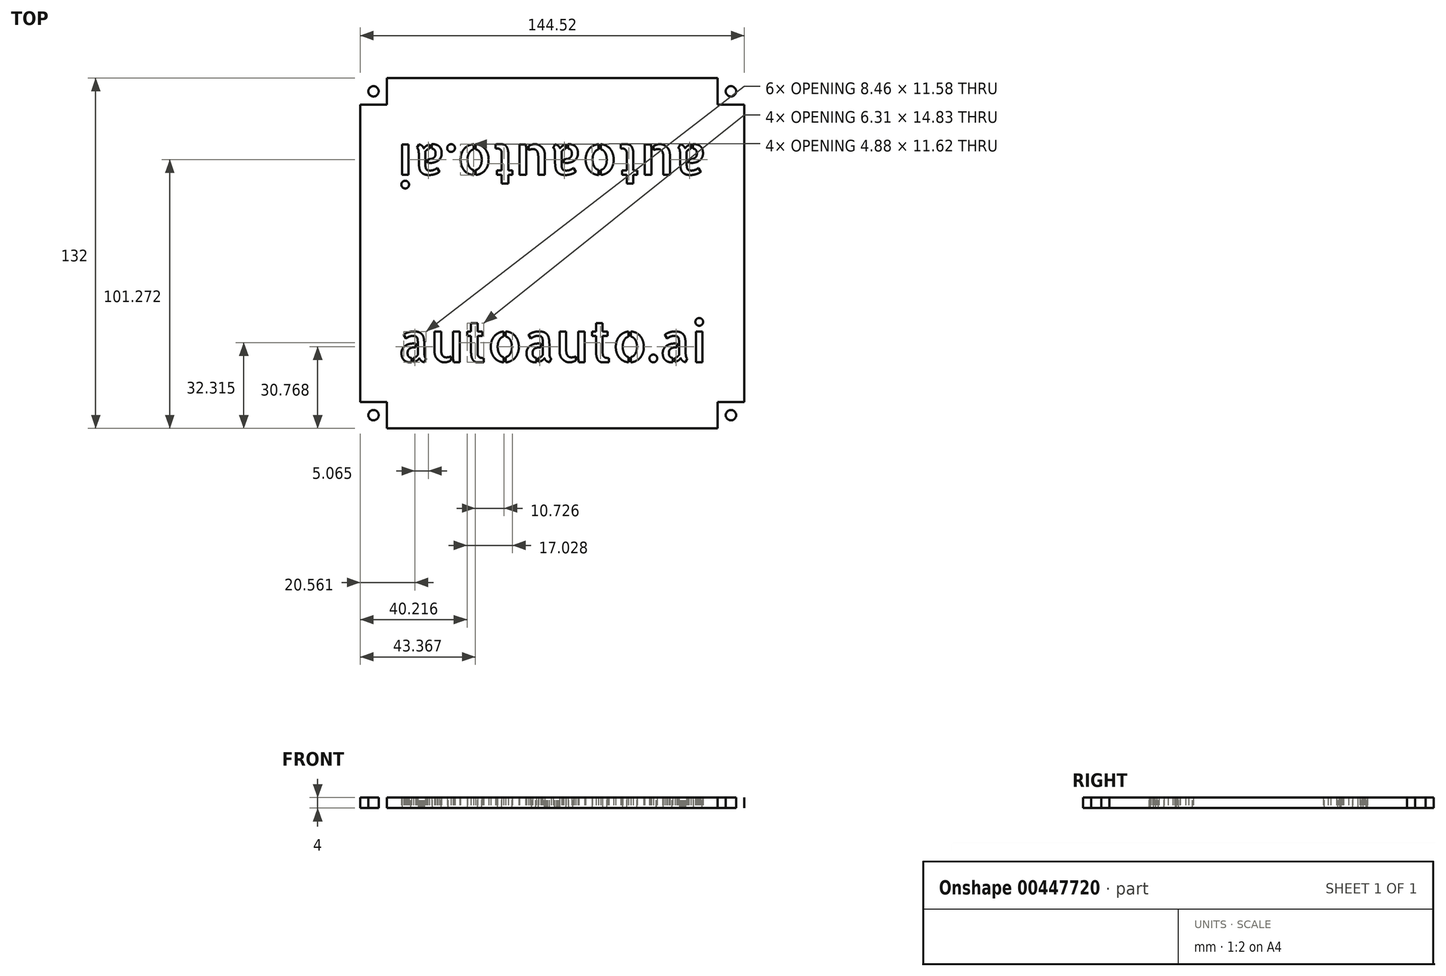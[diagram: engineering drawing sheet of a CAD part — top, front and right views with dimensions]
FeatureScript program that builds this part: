
annotation { "Feature Type Name" : "Feature", "Feature Type Description" : "" }
export const myFeature = defineFeature(function(context is Context, id is Id, definition is map)
    precondition{}
    {
        {
            var Q0;
            Q0=qCreatedBy(makeId("Top.planeOp"),FACE);
            var sketch = newSketch(context, id + "F0", { "sketchPlane" : qUnion([Q0])});
            skLineSegment(sketch, "E0.bottom", {"start": v(-72.26, 66) * mm, "end": v(72.26, 66) * mm});
            skLineSegment(sketch, "E0.top", {"start": v(-72.26, -66) * mm, "end": v(72.26, -66) * mm});
            skLineSegment(sketch, "E0.left", {"start": v(-72.26, 66) * mm, "end": v(-72.26, -66) * mm});
            skLineSegment(sketch, "E0.right", {"start": v(72.26, 66) * mm, "end": v(72.26, -66) * mm});
            skPoint(sketch, "E0.middle", {"position": v(0, 0) * mm});
            skText(sketch, "E1", { "text": "autoauto.ai", "fontName": "AllertaStencil-Regular.ttf"});
            skText(sketch, "E2", { "text": "autoauto.ai", "fontName": "AllertaStencil-Regular.ttf"});
            const initialGuessF0  = {"E1": [-0.05819, -0.041, 1, 0, 0.015], "E2": [0.05819, 0.041, -1, 0, 0.015]};
            skSetInitialGuess(sketch, initialGuessF0);
            skSolve(sketch);
        }
        {
            var Q0;
            Q0=makeQuery(id+"F0.imprint","IMPRINT",FACE,{"disambiguationData":[TD([[makeQuery(id+"F0.imprint","IMPRINT",EDGE,{"derivedFrom":sQuery(id+"F0.wireOp",EDGE,"E0.bottom")}),-1.0]])]});
            extrude(context, id + "F1", {"entities" : qUnion([Q0]), "depth" : 4 * mm});
        }
        {
            var Q0;
            Q0=makeQuery(id+"F1.opExtrude","CAP_FACE",FACE,{"disambiguationData":[OSD([sQuery(id+"F0.wireOp",EDGE,"E0.bottom"),sQuery(id+"F0.wireOp",EDGE,"E0.top"),sQuery(id+"F0.wireOp",EDGE,"E0.left"),sQuery(id+"F0.wireOp",EDGE,"E0.right"),sQuery(id+"F0.wireOp",EDGE,"E1.sketch_text.stroke-0"),sQuery(id+"F0.wireOp",EDGE,"E1.sketch_text.stroke-1"),sQuery(id+"F0.wireOp",EDGE,"E1.sketch_text.stroke-2"),sQuery(id+"F0.wireOp",EDGE,"E1.sketch_text.stroke-3"),sQuery(id+"F0.wireOp",EDGE,"E1.sketch_text.stroke-4"),sQuery(id+"F0.wireOp",EDGE,"E1.sketch_text.stroke-5"),sQuery(id+"F0.wireOp",EDGE,"E1.sketch_text.stroke-6"),sQuery(id+"F0.wireOp",EDGE,"E1.sketch_text.stroke-7"),sQuery(id+"F0.wireOp",EDGE,"E1.sketch_text.stroke-8"),sQuery(id+"F0.wireOp",EDGE,"E1.sketch_text.stroke-9"),sQuery(id+"F0.wireOp",EDGE,"E1.sketch_text.stroke-10"),sQuery(id+"F0.wireOp",EDGE,"E1.sketch_text.stroke-11"),sQuery(id+"F0.wireOp",EDGE,"E1.sketch_text.stroke-12"),sQuery(id+"F0.wireOp",EDGE,"E1.sketch_text.stroke-13"),sQuery(id+"F0.wireOp",EDGE,"E1.sketch_text.stroke-14"),sQuery(id+"F0.wireOp",EDGE,"E1.sketch_text.stroke-15"),sQuery(id+"F0.wireOp",EDGE,"E1.sketch_text.stroke-16"),sQuery(id+"F0.wireOp",EDGE,"E1.sketch_text.stroke-17"),sQuery(id+"F0.wireOp",EDGE,"E1.sketch_text.stroke-18"),sQuery(id+"F0.wireOp",EDGE,"E1.sketch_text.stroke-19"),sQuery(id+"F0.wireOp",EDGE,"E1.sketch_text.stroke-20"),sQuery(id+"F0.wireOp",EDGE,"E1.sketch_text.stroke-21"),sQuery(id+"F0.wireOp",EDGE,"E1.sketch_text.stroke-22"),sQuery(id+"F0.wireOp",EDGE,"E1.sketch_text.stroke-23"),sQuery(id+"F0.wireOp",EDGE,"E1.sketch_text.stroke-24"),sQuery(id+"F0.wireOp",EDGE,"E1.sketch_text.stroke-25"),sQuery(id+"F0.wireOp",EDGE,"E1.sketch_text.stroke-26"),sQuery(id+"F0.wireOp",EDGE,"E1.sketch_text.stroke-27"),sQuery(id+"F0.wireOp",EDGE,"E1.sketch_text.stroke-28"),sQuery(id+"F0.wireOp",EDGE,"E1.sketch_text.stroke-29"),sQuery(id+"F0.wireOp",EDGE,"E1.sketch_text.stroke-30"),sQuery(id+"F0.wireOp",EDGE,"E1.sketch_text.stroke-31"),sQuery(id+"F0.wireOp",EDGE,"E1.sketch_text.stroke-32"),sQuery(id+"F0.wireOp",EDGE,"E1.sketch_text.stroke-33"),sQuery(id+"F0.wireOp",EDGE,"E1.sketch_text.stroke-34"),sQuery(id+"F0.wireOp",EDGE,"E1.sketch_text.stroke-35"),sQuery(id+"F0.wireOp",EDGE,"E1.sketch_text.stroke-36"),sQuery(id+"F0.wireOp",EDGE,"E1.sketch_text.stroke-37"),sQuery(id+"F0.wireOp",EDGE,"E1.sketch_text.stroke-38"),sQuery(id+"F0.wireOp",EDGE,"E1.sketch_text.stroke-39"),sQuery(id+"F0.wireOp",EDGE,"E1.sketch_text.stroke-40"),sQuery(id+"F0.wireOp",EDGE,"E1.sketch_text.stroke-41"),sQuery(id+"F0.wireOp",EDGE,"E1.sketch_text.stroke-42"),sQuery(id+"F0.wireOp",EDGE,"E1.sketch_text.stroke-43"),sQuery(id+"F0.wireOp",EDGE,"E1.sketch_text.stroke-44"),sQuery(id+"F0.wireOp",EDGE,"E1.sketch_text.stroke-45"),sQuery(id+"F0.wireOp",EDGE,"E1.sketch_text.stroke-46"),sQuery(id+"F0.wireOp",EDGE,"E1.sketch_text.stroke-47"),sQuery(id+"F0.wireOp",EDGE,"E1.sketch_text.stroke-48"),sQuery(id+"F0.wireOp",EDGE,"E1.sketch_text.stroke-49"),sQuery(id+"F0.wireOp",EDGE,"E1.sketch_text.stroke-50"),sQuery(id+"F0.wireOp",EDGE,"E1.sketch_text.stroke-51"),sQuery(id+"F0.wireOp",EDGE,"E1.sketch_text.stroke-52"),sQuery(id+"F0.wireOp",EDGE,"E1.sketch_text.stroke-53"),sQuery(id+"F0.wireOp",EDGE,"E1.sketch_text.stroke-54"),sQuery(id+"F0.wireOp",EDGE,"E1.sketch_text.stroke-55"),sQuery(id+"F0.wireOp",EDGE,"E1.sketch_text.stroke-56"),sQuery(id+"F0.wireOp",EDGE,"E1.sketch_text.stroke-57"),sQuery(id+"F0.wireOp",EDGE,"E1.sketch_text.stroke-58"),sQuery(id+"F0.wireOp",EDGE,"E1.sketch_text.stroke-59"),sQuery(id+"F0.wireOp",EDGE,"E1.sketch_text.stroke-60"),sQuery(id+"F0.wireOp",EDGE,"E1.sketch_text.stroke-61"),sQuery(id+"F0.wireOp",EDGE,"E1.sketch_text.stroke-62"),sQuery(id+"F0.wireOp",EDGE,"E1.sketch_text.stroke-63"),sQuery(id+"F0.wireOp",EDGE,"E1.sketch_text.stroke-64"),sQuery(id+"F0.wireOp",EDGE,"E1.sketch_text.stroke-65"),sQuery(id+"F0.wireOp",EDGE,"E1.sketch_text.stroke-66"),sQuery(id+"F0.wireOp",EDGE,"E1.sketch_text.stroke-67"),sQuery(id+"F0.wireOp",EDGE,"E1.sketch_text.stroke-68"),sQuery(id+"F0.wireOp",EDGE,"E1.sketch_text.stroke-69"),sQuery(id+"F0.wireOp",EDGE,"E1.sketch_text.stroke-70"),sQuery(id+"F0.wireOp",EDGE,"E1.sketch_text.stroke-71"),sQuery(id+"F0.wireOp",EDGE,"E1.sketch_text.stroke-72"),sQuery(id+"F0.wireOp",EDGE,"E1.sketch_text.stroke-73"),sQuery(id+"F0.wireOp",EDGE,"E1.sketch_text.stroke-74"),sQuery(id+"F0.wireOp",EDGE,"E1.sketch_text.stroke-75"),sQuery(id+"F0.wireOp",EDGE,"E1.sketch_text.stroke-76"),sQuery(id+"F0.wireOp",EDGE,"E1.sketch_text.stroke-77"),sQuery(id+"F0.wireOp",EDGE,"E1.sketch_text.stroke-78"),sQuery(id+"F0.wireOp",EDGE,"E1.sketch_text.stroke-79"),sQuery(id+"F0.wireOp",EDGE,"E1.sketch_text.stroke-80"),sQuery(id+"F0.wireOp",EDGE,"E1.sketch_text.stroke-81"),sQuery(id+"F0.wireOp",EDGE,"E1.sketch_text.stroke-82"),sQuery(id+"F0.wireOp",EDGE,"E1.sketch_text.stroke-83"),sQuery(id+"F0.wireOp",EDGE,"E1.sketch_text.stroke-84"),sQuery(id+"F0.wireOp",EDGE,"E1.sketch_text.stroke-85"),sQuery(id+"F0.wireOp",EDGE,"E1.sketch_text.stroke-86"),sQuery(id+"F0.wireOp",EDGE,"E1.sketch_text.stroke-87"),sQuery(id+"F0.wireOp",EDGE,"E1.sketch_text.stroke-88"),sQuery(id+"F0.wireOp",EDGE,"E1.sketch_text.stroke-89"),sQuery(id+"F0.wireOp",EDGE,"E1.sketch_text.stroke-90"),sQuery(id+"F0.wireOp",EDGE,"E1.sketch_text.stroke-91"),sQuery(id+"F0.wireOp",EDGE,"E1.sketch_text.stroke-92"),sQuery(id+"F0.wireOp",EDGE,"E1.sketch_text.stroke-93"),sQuery(id+"F0.wireOp",EDGE,"E1.sketch_text.stroke-94"),sQuery(id+"F0.wireOp",EDGE,"E1.sketch_text.stroke-95"),sQuery(id+"F0.wireOp",EDGE,"E1.sketch_text.stroke-96"),sQuery(id+"F0.wireOp",EDGE,"E1.sketch_text.stroke-97"),sQuery(id+"F0.wireOp",EDGE,"E1.sketch_text.stroke-98"),sQuery(id+"F0.wireOp",EDGE,"E1.sketch_text.stroke-99"),sQuery(id+"F0.wireOp",EDGE,"E1.sketch_text.stroke-100"),sQuery(id+"F0.wireOp",EDGE,"E1.sketch_text.stroke-101"),sQuery(id+"F0.wireOp",EDGE,"E1.sketch_text.stroke-102"),sQuery(id+"F0.wireOp",EDGE,"E1.sketch_text.stroke-103"),sQuery(id+"F0.wireOp",EDGE,"E1.sketch_text.stroke-104"),sQuery(id+"F0.wireOp",EDGE,"E1.sketch_text.stroke-105"),sQuery(id+"F0.wireOp",EDGE,"E1.sketch_text.stroke-106"),sQuery(id+"F0.wireOp",EDGE,"E1.sketch_text.stroke-107"),sQuery(id+"F0.wireOp",EDGE,"E1.sketch_text.stroke-108"),sQuery(id+"F0.wireOp",EDGE,"E1.sketch_text.stroke-109"),sQuery(id+"F0.wireOp",EDGE,"E1.sketch_text.stroke-110"),sQuery(id+"F0.wireOp",EDGE,"E1.sketch_text.stroke-111"),sQuery(id+"F0.wireOp",EDGE,"E1.sketch_text.stroke-112"),sQuery(id+"F0.wireOp",EDGE,"E1.sketch_text.stroke-113"),sQuery(id+"F0.wireOp",EDGE,"E1.sketch_text.stroke-114"),sQuery(id+"F0.wireOp",EDGE,"E1.sketch_text.stroke-115"),sQuery(id+"F0.wireOp",EDGE,"E1.sketch_text.stroke-116"),sQuery(id+"F0.wireOp",EDGE,"E1.sketch_text.stroke-117"),sQuery(id+"F0.wireOp",EDGE,"E1.sketch_text.stroke-118"),sQuery(id+"F0.wireOp",EDGE,"E1.sketch_text.stroke-119"),sQuery(id+"F0.wireOp",EDGE,"E1.sketch_text.stroke-120"),sQuery(id+"F0.wireOp",EDGE,"E1.sketch_text.stroke-121"),sQuery(id+"F0.wireOp",EDGE,"E1.sketch_text.stroke-122"),sQuery(id+"F0.wireOp",EDGE,"E1.sketch_text.stroke-123"),sQuery(id+"F0.wireOp",EDGE,"E1.sketch_text.stroke-124"),sQuery(id+"F0.wireOp",EDGE,"E1.sketch_text.stroke-125"),sQuery(id+"F0.wireOp",EDGE,"E1.sketch_text.stroke-126"),sQuery(id+"F0.wireOp",EDGE,"E1.sketch_text.stroke-127"),sQuery(id+"F0.wireOp",EDGE,"E1.sketch_text.stroke-128"),sQuery(id+"F0.wireOp",EDGE,"E1.sketch_text.stroke-129"),sQuery(id+"F0.wireOp",EDGE,"E1.sketch_text.stroke-130"),sQuery(id+"F0.wireOp",EDGE,"E1.sketch_text.stroke-131"),sQuery(id+"F0.wireOp",EDGE,"E1.sketch_text.stroke-132"),sQuery(id+"F0.wireOp",EDGE,"E1.sketch_text.stroke-133"),sQuery(id+"F0.wireOp",EDGE,"E1.sketch_text.stroke-134"),sQuery(id+"F0.wireOp",EDGE,"E1.sketch_text.stroke-135"),sQuery(id+"F0.wireOp",EDGE,"E1.sketch_text.stroke-136"),sQuery(id+"F0.wireOp",EDGE,"E1.sketch_text.stroke-137"),sQuery(id+"F0.wireOp",EDGE,"E1.sketch_text.stroke-138"),sQuery(id+"F0.wireOp",EDGE,"E1.sketch_text.stroke-139"),sQuery(id+"F0.wireOp",EDGE,"E1.sketch_text.stroke-140"),sQuery(id+"F0.wireOp",EDGE,"E1.sketch_text.stroke-141"),sQuery(id+"F0.wireOp",EDGE,"E1.sketch_text.stroke-142"),sQuery(id+"F0.wireOp",EDGE,"E1.sketch_text.stroke-143"),sQuery(id+"F0.wireOp",EDGE,"E1.sketch_text.stroke-144"),sQuery(id+"F0.wireOp",EDGE,"E1.sketch_text.stroke-145"),sQuery(id+"F0.wireOp",EDGE,"E1.sketch_text.stroke-146"),sQuery(id+"F0.wireOp",EDGE,"E1.sketch_text.stroke-147"),sQuery(id+"F0.wireOp",EDGE,"E1.sketch_text.stroke-148"),sQuery(id+"F0.wireOp",EDGE,"E1.sketch_text.stroke-149"),sQuery(id+"F0.wireOp",EDGE,"E1.sketch_text.stroke-150"),sQuery(id+"F0.wireOp",EDGE,"E1.sketch_text.stroke-151"),sQuery(id+"F0.wireOp",EDGE,"E1.sketch_text.stroke-152"),sQuery(id+"F0.wireOp",EDGE,"E1.sketch_text.stroke-153"),sQuery(id+"F0.wireOp",EDGE,"E1.sketch_text.stroke-154"),sQuery(id+"F0.wireOp",EDGE,"E1.sketch_text.stroke-155"),sQuery(id+"F0.wireOp",EDGE,"E1.sketch_text.stroke-156"),sQuery(id+"F0.wireOp",EDGE,"E1.sketch_text.stroke-157"),sQuery(id+"F0.wireOp",EDGE,"E1.sketch_text.stroke-158"),sQuery(id+"F0.wireOp",EDGE,"E1.sketch_text.stroke-159"),sQuery(id+"F0.wireOp",EDGE,"E1.sketch_text.stroke-160"),sQuery(id+"F0.wireOp",EDGE,"E1.sketch_text.stroke-161"),sQuery(id+"F0.wireOp",EDGE,"E1.sketch_text.stroke-162"),sQuery(id+"F0.wireOp",EDGE,"E1.sketch_text.stroke-163"),sQuery(id+"F0.wireOp",EDGE,"E1.sketch_text.stroke-164"),sQuery(id+"F0.wireOp",EDGE,"E1.sketch_text.stroke-165"),sQuery(id+"F0.wireOp",EDGE,"E1.sketch_text.stroke-166"),sQuery(id+"F0.wireOp",EDGE,"E1.sketch_text.stroke-167"),sQuery(id+"F0.wireOp",EDGE,"E1.sketch_text.stroke-168"),sQuery(id+"F0.wireOp",EDGE,"E1.sketch_text.stroke-169"),sQuery(id+"F0.wireOp",EDGE,"E1.sketch_text.stroke-170"),sQuery(id+"F0.wireOp",EDGE,"E1.sketch_text.stroke-171"),sQuery(id+"F0.wireOp",EDGE,"E1.sketch_text.stroke-172"),sQuery(id+"F0.wireOp",EDGE,"E1.sketch_text.stroke-173"),sQuery(id+"F0.wireOp",EDGE,"E1.sketch_text.stroke-174"),sQuery(id+"F0.wireOp",EDGE,"E1.sketch_text.stroke-175"),sQuery(id+"F0.wireOp",EDGE,"E1.sketch_text.stroke-176"),sQuery(id+"F0.wireOp",EDGE,"E1.sketch_text.stroke-177"),sQuery(id+"F0.wireOp",EDGE,"E1.sketch_text.stroke-178"),sQuery(id+"F0.wireOp",EDGE,"E1.sketch_text.stroke-179"),sQuery(id+"F0.wireOp",EDGE,"E1.sketch_text.stroke-180"),sQuery(id+"F0.wireOp",EDGE,"E1.sketch_text.stroke-181"),sQuery(id+"F0.wireOp",EDGE,"E1.sketch_text.stroke-182"),sQuery(id+"F0.wireOp",EDGE,"E1.sketch_text.stroke-183"),sQuery(id+"F0.wireOp",EDGE,"E1.sketch_text.stroke-184"),sQuery(id+"F0.wireOp",EDGE,"E1.sketch_text.stroke-185"),sQuery(id+"F0.wireOp",EDGE,"E1.sketch_text.stroke-186"),sQuery(id+"F0.wireOp",EDGE,"E1.sketch_text.stroke-187"),sQuery(id+"F0.wireOp",EDGE,"E1.sketch_text.stroke-188"),sQuery(id+"F0.wireOp",EDGE,"E1.sketch_text.stroke-189"),sQuery(id+"F0.wireOp",EDGE,"E1.sketch_text.stroke-190"),sQuery(id+"F0.wireOp",EDGE,"E1.sketch_text.stroke-191"),sQuery(id+"F0.wireOp",EDGE,"E1.sketch_text.stroke-192"),sQuery(id+"F0.wireOp",EDGE,"E1.sketch_text.stroke-193"),sQuery(id+"F0.wireOp",EDGE,"E1.sketch_text.stroke-194"),sQuery(id+"F0.wireOp",EDGE,"E1.sketch_text.stroke-195"),sQuery(id+"F0.wireOp",EDGE,"E1.sketch_text.stroke-196"),sQuery(id+"F0.wireOp",EDGE,"E1.sketch_text.stroke-197"),sQuery(id+"F0.wireOp",EDGE,"E1.sketch_text.stroke-198"),sQuery(id+"F0.wireOp",EDGE,"E1.sketch_text.stroke-199"),sQuery(id+"F0.wireOp",EDGE,"E1.sketch_text.stroke-200"),sQuery(id+"F0.wireOp",EDGE,"E1.sketch_text.stroke-201"),sQuery(id+"F0.wireOp",EDGE,"E1.sketch_text.stroke-202"),sQuery(id+"F0.wireOp",EDGE,"E1.sketch_text.stroke-203"),sQuery(id+"F0.wireOp",EDGE,"E1.sketch_text.stroke-204"),sQuery(id+"F0.wireOp",EDGE,"E1.sketch_text.stroke-205"),sQuery(id+"F0.wireOp",EDGE,"E1.sketch_text.stroke-206"),sQuery(id+"F0.wireOp",EDGE,"E1.sketch_text.stroke-207"),sQuery(id+"F0.wireOp",EDGE,"E1.sketch_text.stroke-208"),sQuery(id+"F0.wireOp",EDGE,"E1.sketch_text.stroke-209"),sQuery(id+"F0.wireOp",EDGE,"E1.sketch_text.stroke-210"),sQuery(id+"F0.wireOp",EDGE,"E1.sketch_text.stroke-211"),sQuery(id+"F0.wireOp",EDGE,"E1.sketch_text.stroke-212"),sQuery(id+"F0.wireOp",EDGE,"E1.sketch_text.stroke-213"),sQuery(id+"F0.wireOp",EDGE,"E1.sketch_text.stroke-214"),sQuery(id+"F0.wireOp",EDGE,"E1.sketch_text.stroke-215"),sQuery(id+"F0.wireOp",EDGE,"E1.sketch_text.stroke-216"),sQuery(id+"F0.wireOp",EDGE,"E1.sketch_text.stroke-217"),sQuery(id+"F0.wireOp",EDGE,"E1.sketch_text.stroke-218"),sQuery(id+"F0.wireOp",EDGE,"E1.sketch_text.stroke-219"),sQuery(id+"F0.wireOp",EDGE,"E1.sketch_text.stroke-220"),sQuery(id+"F0.wireOp",EDGE,"E1.sketch_text.stroke-221"),sQuery(id+"F0.wireOp",EDGE,"E1.sketch_text.stroke-222"),sQuery(id+"F0.wireOp",EDGE,"E1.sketch_text.stroke-223"),sQuery(id+"F0.wireOp",EDGE,"E1.sketch_text.stroke-224"),sQuery(id+"F0.wireOp",EDGE,"E1.sketch_text.stroke-225"),sQuery(id+"F0.wireOp",EDGE,"E1.sketch_text.stroke-226"),sQuery(id+"F0.wireOp",EDGE,"E1.sketch_text.stroke-227"),sQuery(id+"F0.wireOp",EDGE,"E1.sketch_text.stroke-228"),sQuery(id+"F0.wireOp",EDGE,"E1.sketch_text.stroke-229"),sQuery(id+"F0.wireOp",EDGE,"E1.sketch_text.stroke-230"),sQuery(id+"F0.wireOp",EDGE,"E1.sketch_text.stroke-231"),sQuery(id+"F0.wireOp",EDGE,"E1.sketch_text.stroke-232"),sQuery(id+"F0.wireOp",EDGE,"E1.sketch_text.stroke-233"),sQuery(id+"F0.wireOp",EDGE,"E1.sketch_text.stroke-234"),sQuery(id+"F0.wireOp",EDGE,"E1.sketch_text.stroke-235"),sQuery(id+"F0.wireOp",EDGE,"E1.sketch_text.stroke-236"),sQuery(id+"F0.wireOp",EDGE,"E1.sketch_text.stroke-237"),sQuery(id+"F0.wireOp",EDGE,"E1.sketch_text.stroke-238"),sQuery(id+"F0.wireOp",EDGE,"E1.sketch_text.stroke-239"),sQuery(id+"F0.wireOp",EDGE,"E1.sketch_text.stroke-240"),sQuery(id+"F0.wireOp",EDGE,"E1.sketch_text.stroke-241"),sQuery(id+"F0.wireOp",EDGE,"E1.sketch_text.stroke-242"),sQuery(id+"F0.wireOp",EDGE,"E1.sketch_text.stroke-243"),sQuery(id+"F0.wireOp",EDGE,"E1.sketch_text.stroke-244"),sQuery(id+"F0.wireOp",EDGE,"E1.sketch_text.stroke-245"),sQuery(id+"F0.wireOp",EDGE,"E1.sketch_text.stroke-246"),sQuery(id+"F0.wireOp",EDGE,"E1.sketch_text.stroke-247"),sQuery(id+"F0.wireOp",EDGE,"E1.sketch_text.stroke-248"),sQuery(id+"F0.wireOp",EDGE,"E1.sketch_text.stroke-249"),sQuery(id+"F0.wireOp",EDGE,"E1.sketch_text.stroke-250"),sQuery(id+"F0.wireOp",EDGE,"E1.sketch_text.stroke-251"),sQuery(id+"F0.wireOp",EDGE,"E1.sketch_text.stroke-252"),sQuery(id+"F0.wireOp",EDGE,"E1.sketch_text.stroke-253"),sQuery(id+"F0.wireOp",EDGE,"E1.sketch_text.stroke-254"),sQuery(id+"F0.wireOp",EDGE,"E1.sketch_text.stroke-255"),sQuery(id+"F0.wireOp",EDGE,"E1.sketch_text.stroke-256"),sQuery(id+"F0.wireOp",EDGE,"E1.sketch_text.stroke-257"),sQuery(id+"F0.wireOp",EDGE,"E1.sketch_text.stroke-258"),sQuery(id+"F0.wireOp",EDGE,"E1.sketch_text.stroke-259"),sQuery(id+"F0.wireOp",EDGE,"E1.sketch_text.stroke-260"),sQuery(id+"F0.wireOp",EDGE,"E1.sketch_text.stroke-261"),sQuery(id+"F0.wireOp",EDGE,"E1.sketch_text.stroke-262"),sQuery(id+"F0.wireOp",EDGE,"E1.sketch_text.stroke-263"),sQuery(id+"F0.wireOp",EDGE,"E1.sketch_text.stroke-264"),sQuery(id+"F0.wireOp",EDGE,"E1.sketch_text.stroke-265"),sQuery(id+"F0.wireOp",EDGE,"E1.sketch_text.stroke-266"),sQuery(id+"F0.wireOp",EDGE,"E1.sketch_text.stroke-267"),sQuery(id+"F0.wireOp",EDGE,"E1.sketch_text.stroke-268"),sQuery(id+"F0.wireOp",EDGE,"E1.sketch_text.stroke-269"),sQuery(id+"F0.wireOp",EDGE,"E1.sketch_text.stroke-270"),sQuery(id+"F0.wireOp",EDGE,"E1.sketch_text.stroke-271"),sQuery(id+"F0.wireOp",EDGE,"E1.sketch_text.stroke-272"),sQuery(id+"F0.wireOp",EDGE,"E1.sketch_text.stroke-273"),sQuery(id+"F0.wireOp",EDGE,"E1.sketch_text.stroke-274"),sQuery(id+"F0.wireOp",EDGE,"E1.sketch_text.stroke-275"),sQuery(id+"F0.wireOp",EDGE,"E1.sketch_text.stroke-276"),sQuery(id+"F0.wireOp",EDGE,"E1.sketch_text.stroke-277"),sQuery(id+"F0.wireOp",EDGE,"E1.sketch_text.stroke-278"),sQuery(id+"F0.wireOp",EDGE,"E1.sketch_text.stroke-279"),sQuery(id+"F0.wireOp",EDGE,"E1.sketch_text.stroke-280"),sQuery(id+"F0.wireOp",EDGE,"E1.sketch_text.stroke-281"),sQuery(id+"F0.wireOp",EDGE,"E1.sketch_text.stroke-282"),sQuery(id+"F0.wireOp",EDGE,"E1.sketch_text.stroke-283"),sQuery(id+"F0.wireOp",EDGE,"E1.sketch_text.stroke-284"),sQuery(id+"F0.wireOp",EDGE,"E1.sketch_text.stroke-285"),sQuery(id+"F0.wireOp",EDGE,"E1.sketch_text.stroke-286"),sQuery(id+"F0.wireOp",EDGE,"E1.sketch_text.stroke-287"),sQuery(id+"F0.wireOp",EDGE,"E1.sketch_text.stroke-288"),sQuery(id+"F0.wireOp",EDGE,"E1.sketch_text.stroke-289"),sQuery(id+"F0.wireOp",EDGE,"E1.sketch_text.stroke-290"),sQuery(id+"F0.wireOp",EDGE,"E1.sketch_text.stroke-291"),sQuery(id+"F0.wireOp",EDGE,"E1.sketch_text.stroke-292"),sQuery(id+"F0.wireOp",EDGE,"E1.sketch_text.stroke-293"),sQuery(id+"F0.wireOp",EDGE,"E1.sketch_text.stroke-294"),sQuery(id+"F0.wireOp",EDGE,"E1.sketch_text.stroke-295"),sQuery(id+"F0.wireOp",EDGE,"E1.sketch_text.stroke-296"),sQuery(id+"F0.wireOp",EDGE,"E1.sketch_text.stroke-297"),sQuery(id+"F0.wireOp",EDGE,"E1.sketch_text.stroke-298"),sQuery(id+"F0.wireOp",EDGE,"E1.sketch_text.stroke-299"),sQuery(id+"F0.wireOp",EDGE,"E1.sketch_text.stroke-300"),sQuery(id+"F0.wireOp",EDGE,"E1.sketch_text.stroke-301"),sQuery(id+"F0.wireOp",EDGE,"E1.sketch_text.stroke-302"),sQuery(id+"F0.wireOp",EDGE,"E1.sketch_text.stroke-303"),sQuery(id+"F0.wireOp",EDGE,"E1.sketch_text.stroke-304"),sQuery(id+"F0.wireOp",EDGE,"E1.sketch_text.stroke-305"),sQuery(id+"F0.wireOp",EDGE,"E1.sketch_text.stroke-306"),sQuery(id+"F0.wireOp",EDGE,"E1.sketch_text.stroke-307"),sQuery(id+"F0.wireOp",EDGE,"E1.sketch_text.stroke-308"),sQuery(id+"F0.wireOp",EDGE,"E1.sketch_text.stroke-309"),sQuery(id+"F0.wireOp",EDGE,"E1.sketch_text.stroke-310"),sQuery(id+"F0.wireOp",EDGE,"E1.sketch_text.stroke-311"),sQuery(id+"F0.wireOp",EDGE,"E1.sketch_text.stroke-312"),sQuery(id+"F0.wireOp",EDGE,"E1.sketch_text.stroke-313"),sQuery(id+"F0.wireOp",EDGE,"E1.sketch_text.stroke-314"),sQuery(id+"F0.wireOp",EDGE,"E1.sketch_text.stroke-315"),sQuery(id+"F0.wireOp",EDGE,"E1.sketch_text.stroke-316"),sQuery(id+"F0.wireOp",EDGE,"E1.sketch_text.stroke-317"),sQuery(id+"F0.wireOp",EDGE,"E1.sketch_text.stroke-318"),sQuery(id+"F0.wireOp",EDGE,"E1.sketch_text.stroke-319"),sQuery(id+"F0.wireOp",EDGE,"E1.sketch_text.stroke-320"),sQuery(id+"F0.wireOp",EDGE,"E1.sketch_text.stroke-321"),sQuery(id+"F0.wireOp",EDGE,"E1.sketch_text.stroke-322"),sQuery(id+"F0.wireOp",EDGE,"E1.sketch_text.stroke-323"),sQuery(id+"F0.wireOp",EDGE,"E1.sketch_text.stroke-324"),sQuery(id+"F0.wireOp",EDGE,"E1.sketch_text.stroke-325"),sQuery(id+"F0.wireOp",EDGE,"E1.sketch_text.stroke-326"),sQuery(id+"F0.wireOp",EDGE,"E1.sketch_text.stroke-327"),sQuery(id+"F0.wireOp",EDGE,"E1.sketch_text.stroke-328"),sQuery(id+"F0.wireOp",EDGE,"E1.sketch_text.stroke-329"),sQuery(id+"F0.wireOp",EDGE,"E1.sketch_text.stroke-330"),sQuery(id+"F0.wireOp",EDGE,"E1.sketch_text.stroke-331"),sQuery(id+"F0.wireOp",EDGE,"E1.sketch_text.stroke-332"),sQuery(id+"F0.wireOp",EDGE,"E1.sketch_text.stroke-333"),sQuery(id+"F0.wireOp",EDGE,"E1.sketch_text.stroke-334"),sQuery(id+"F0.wireOp",EDGE,"E1.sketch_text.stroke-335"),sQuery(id+"F0.wireOp",EDGE,"E1.sketch_text.stroke-336"),sQuery(id+"F0.wireOp",EDGE,"E1.sketch_text.stroke-337"),sQuery(id+"F0.wireOp",EDGE,"E1.sketch_text.stroke-338"),sQuery(id+"F0.wireOp",EDGE,"E1.sketch_text.stroke-339"),sQuery(id+"F0.wireOp",EDGE,"E1.sketch_text.stroke-340"),sQuery(id+"F0.wireOp",EDGE,"E1.sketch_text.stroke-341"),sQuery(id+"F0.wireOp",EDGE,"E1.sketch_text.stroke-342"),sQuery(id+"F0.wireOp",EDGE,"E1.sketch_text.stroke-343"),sQuery(id+"F0.wireOp",EDGE,"E1.sketch_text.stroke-344"),sQuery(id+"F0.wireOp",EDGE,"E1.sketch_text.stroke-345"),sQuery(id+"F0.wireOp",EDGE,"E1.sketch_text.stroke-346"),sQuery(id+"F0.wireOp",EDGE,"E1.sketch_text.stroke-347"),sQuery(id+"F0.wireOp",EDGE,"E1.sketch_text.stroke-348"),sQuery(id+"F0.wireOp",EDGE,"E2.sketch_text.stroke-0"),sQuery(id+"F0.wireOp",EDGE,"E2.sketch_text.stroke-1"),sQuery(id+"F0.wireOp",EDGE,"E2.sketch_text.stroke-2"),sQuery(id+"F0.wireOp",EDGE,"E2.sketch_text.stroke-3"),sQuery(id+"F0.wireOp",EDGE,"E2.sketch_text.stroke-4"),sQuery(id+"F0.wireOp",EDGE,"E2.sketch_text.stroke-5"),sQuery(id+"F0.wireOp",EDGE,"E2.sketch_text.stroke-6"),sQuery(id+"F0.wireOp",EDGE,"E2.sketch_text.stroke-7"),sQuery(id+"F0.wireOp",EDGE,"E2.sketch_text.stroke-8"),sQuery(id+"F0.wireOp",EDGE,"E2.sketch_text.stroke-9"),sQuery(id+"F0.wireOp",EDGE,"E2.sketch_text.stroke-10"),sQuery(id+"F0.wireOp",EDGE,"E2.sketch_text.stroke-11"),sQuery(id+"F0.wireOp",EDGE,"E2.sketch_text.stroke-12"),sQuery(id+"F0.wireOp",EDGE,"E2.sketch_text.stroke-13"),sQuery(id+"F0.wireOp",EDGE,"E2.sketch_text.stroke-14"),sQuery(id+"F0.wireOp",EDGE,"E2.sketch_text.stroke-15"),sQuery(id+"F0.wireOp",EDGE,"E2.sketch_text.stroke-16"),sQuery(id+"F0.wireOp",EDGE,"E2.sketch_text.stroke-17"),sQuery(id+"F0.wireOp",EDGE,"E2.sketch_text.stroke-18"),sQuery(id+"F0.wireOp",EDGE,"E2.sketch_text.stroke-19"),sQuery(id+"F0.wireOp",EDGE,"E2.sketch_text.stroke-20"),sQuery(id+"F0.wireOp",EDGE,"E2.sketch_text.stroke-21"),sQuery(id+"F0.wireOp",EDGE,"E2.sketch_text.stroke-22"),sQuery(id+"F0.wireOp",EDGE,"E2.sketch_text.stroke-23"),sQuery(id+"F0.wireOp",EDGE,"E2.sketch_text.stroke-24"),sQuery(id+"F0.wireOp",EDGE,"E2.sketch_text.stroke-25"),sQuery(id+"F0.wireOp",EDGE,"E2.sketch_text.stroke-26"),sQuery(id+"F0.wireOp",EDGE,"E2.sketch_text.stroke-27"),sQuery(id+"F0.wireOp",EDGE,"E2.sketch_text.stroke-28"),sQuery(id+"F0.wireOp",EDGE,"E2.sketch_text.stroke-29"),sQuery(id+"F0.wireOp",EDGE,"E2.sketch_text.stroke-30"),sQuery(id+"F0.wireOp",EDGE,"E2.sketch_text.stroke-31"),sQuery(id+"F0.wireOp",EDGE,"E2.sketch_text.stroke-32"),sQuery(id+"F0.wireOp",EDGE,"E2.sketch_text.stroke-33"),sQuery(id+"F0.wireOp",EDGE,"E2.sketch_text.stroke-34"),sQuery(id+"F0.wireOp",EDGE,"E2.sketch_text.stroke-35"),sQuery(id+"F0.wireOp",EDGE,"E2.sketch_text.stroke-36"),sQuery(id+"F0.wireOp",EDGE,"E2.sketch_text.stroke-37"),sQuery(id+"F0.wireOp",EDGE,"E2.sketch_text.stroke-38"),sQuery(id+"F0.wireOp",EDGE,"E2.sketch_text.stroke-39"),sQuery(id+"F0.wireOp",EDGE,"E2.sketch_text.stroke-40"),sQuery(id+"F0.wireOp",EDGE,"E2.sketch_text.stroke-41"),sQuery(id+"F0.wireOp",EDGE,"E2.sketch_text.stroke-42"),sQuery(id+"F0.wireOp",EDGE,"E2.sketch_text.stroke-43"),sQuery(id+"F0.wireOp",EDGE,"E2.sketch_text.stroke-44"),sQuery(id+"F0.wireOp",EDGE,"E2.sketch_text.stroke-45"),sQuery(id+"F0.wireOp",EDGE,"E2.sketch_text.stroke-46"),sQuery(id+"F0.wireOp",EDGE,"E2.sketch_text.stroke-47"),sQuery(id+"F0.wireOp",EDGE,"E2.sketch_text.stroke-48"),sQuery(id+"F0.wireOp",EDGE,"E2.sketch_text.stroke-49"),sQuery(id+"F0.wireOp",EDGE,"E2.sketch_text.stroke-50"),sQuery(id+"F0.wireOp",EDGE,"E2.sketch_text.stroke-51"),sQuery(id+"F0.wireOp",EDGE,"E2.sketch_text.stroke-52"),sQuery(id+"F0.wireOp",EDGE,"E2.sketch_text.stroke-53"),sQuery(id+"F0.wireOp",EDGE,"E2.sketch_text.stroke-54"),sQuery(id+"F0.wireOp",EDGE,"E2.sketch_text.stroke-55"),sQuery(id+"F0.wireOp",EDGE,"E2.sketch_text.stroke-56"),sQuery(id+"F0.wireOp",EDGE,"E2.sketch_text.stroke-57"),sQuery(id+"F0.wireOp",EDGE,"E2.sketch_text.stroke-58"),sQuery(id+"F0.wireOp",EDGE,"E2.sketch_text.stroke-59"),sQuery(id+"F0.wireOp",EDGE,"E2.sketch_text.stroke-60"),sQuery(id+"F0.wireOp",EDGE,"E2.sketch_text.stroke-61"),sQuery(id+"F0.wireOp",EDGE,"E2.sketch_text.stroke-62"),sQuery(id+"F0.wireOp",EDGE,"E2.sketch_text.stroke-63"),sQuery(id+"F0.wireOp",EDGE,"E2.sketch_text.stroke-64"),sQuery(id+"F0.wireOp",EDGE,"E2.sketch_text.stroke-65"),sQuery(id+"F0.wireOp",EDGE,"E2.sketch_text.stroke-66"),sQuery(id+"F0.wireOp",EDGE,"E2.sketch_text.stroke-67"),sQuery(id+"F0.wireOp",EDGE,"E2.sketch_text.stroke-68"),sQuery(id+"F0.wireOp",EDGE,"E2.sketch_text.stroke-69"),sQuery(id+"F0.wireOp",EDGE,"E2.sketch_text.stroke-70"),sQuery(id+"F0.wireOp",EDGE,"E2.sketch_text.stroke-71"),sQuery(id+"F0.wireOp",EDGE,"E2.sketch_text.stroke-72"),sQuery(id+"F0.wireOp",EDGE,"E2.sketch_text.stroke-73"),sQuery(id+"F0.wireOp",EDGE,"E2.sketch_text.stroke-74"),sQuery(id+"F0.wireOp",EDGE,"E2.sketch_text.stroke-75"),sQuery(id+"F0.wireOp",EDGE,"E2.sketch_text.stroke-76"),sQuery(id+"F0.wireOp",EDGE,"E2.sketch_text.stroke-77"),sQuery(id+"F0.wireOp",EDGE,"E2.sketch_text.stroke-78"),sQuery(id+"F0.wireOp",EDGE,"E2.sketch_text.stroke-79"),sQuery(id+"F0.wireOp",EDGE,"E2.sketch_text.stroke-80"),sQuery(id+"F0.wireOp",EDGE,"E2.sketch_text.stroke-81"),sQuery(id+"F0.wireOp",EDGE,"E2.sketch_text.stroke-82"),sQuery(id+"F0.wireOp",EDGE,"E2.sketch_text.stroke-83"),sQuery(id+"F0.wireOp",EDGE,"E2.sketch_text.stroke-84"),sQuery(id+"F0.wireOp",EDGE,"E2.sketch_text.stroke-85"),sQuery(id+"F0.wireOp",EDGE,"E2.sketch_text.stroke-86"),sQuery(id+"F0.wireOp",EDGE,"E2.sketch_text.stroke-87"),sQuery(id+"F0.wireOp",EDGE,"E2.sketch_text.stroke-88"),sQuery(id+"F0.wireOp",EDGE,"E2.sketch_text.stroke-89"),sQuery(id+"F0.wireOp",EDGE,"E2.sketch_text.stroke-90"),sQuery(id+"F0.wireOp",EDGE,"E2.sketch_text.stroke-91"),sQuery(id+"F0.wireOp",EDGE,"E2.sketch_text.stroke-92"),sQuery(id+"F0.wireOp",EDGE,"E2.sketch_text.stroke-93"),sQuery(id+"F0.wireOp",EDGE,"E2.sketch_text.stroke-94"),sQuery(id+"F0.wireOp",EDGE,"E2.sketch_text.stroke-95"),sQuery(id+"F0.wireOp",EDGE,"E2.sketch_text.stroke-96"),sQuery(id+"F0.wireOp",EDGE,"E2.sketch_text.stroke-97"),sQuery(id+"F0.wireOp",EDGE,"E2.sketch_text.stroke-98"),sQuery(id+"F0.wireOp",EDGE,"E2.sketch_text.stroke-99"),sQuery(id+"F0.wireOp",EDGE,"E2.sketch_text.stroke-100"),sQuery(id+"F0.wireOp",EDGE,"E2.sketch_text.stroke-101"),sQuery(id+"F0.wireOp",EDGE,"E2.sketch_text.stroke-102"),sQuery(id+"F0.wireOp",EDGE,"E2.sketch_text.stroke-103"),sQuery(id+"F0.wireOp",EDGE,"E2.sketch_text.stroke-104"),sQuery(id+"F0.wireOp",EDGE,"E2.sketch_text.stroke-105"),sQuery(id+"F0.wireOp",EDGE,"E2.sketch_text.stroke-106"),sQuery(id+"F0.wireOp",EDGE,"E2.sketch_text.stroke-107"),sQuery(id+"F0.wireOp",EDGE,"E2.sketch_text.stroke-108"),sQuery(id+"F0.wireOp",EDGE,"E2.sketch_text.stroke-109"),sQuery(id+"F0.wireOp",EDGE,"E2.sketch_text.stroke-110"),sQuery(id+"F0.wireOp",EDGE,"E2.sketch_text.stroke-111"),sQuery(id+"F0.wireOp",EDGE,"E2.sketch_text.stroke-112"),sQuery(id+"F0.wireOp",EDGE,"E2.sketch_text.stroke-113"),sQuery(id+"F0.wireOp",EDGE,"E2.sketch_text.stroke-114"),sQuery(id+"F0.wireOp",EDGE,"E2.sketch_text.stroke-115"),sQuery(id+"F0.wireOp",EDGE,"E2.sketch_text.stroke-116"),sQuery(id+"F0.wireOp",EDGE,"E2.sketch_text.stroke-117"),sQuery(id+"F0.wireOp",EDGE,"E2.sketch_text.stroke-118"),sQuery(id+"F0.wireOp",EDGE,"E2.sketch_text.stroke-119"),sQuery(id+"F0.wireOp",EDGE,"E2.sketch_text.stroke-120"),sQuery(id+"F0.wireOp",EDGE,"E2.sketch_text.stroke-121"),sQuery(id+"F0.wireOp",EDGE,"E2.sketch_text.stroke-122"),sQuery(id+"F0.wireOp",EDGE,"E2.sketch_text.stroke-123"),sQuery(id+"F0.wireOp",EDGE,"E2.sketch_text.stroke-124"),sQuery(id+"F0.wireOp",EDGE,"E2.sketch_text.stroke-125"),sQuery(id+"F0.wireOp",EDGE,"E2.sketch_text.stroke-126"),sQuery(id+"F0.wireOp",EDGE,"E2.sketch_text.stroke-127"),sQuery(id+"F0.wireOp",EDGE,"E2.sketch_text.stroke-128"),sQuery(id+"F0.wireOp",EDGE,"E2.sketch_text.stroke-129"),sQuery(id+"F0.wireOp",EDGE,"E2.sketch_text.stroke-130"),sQuery(id+"F0.wireOp",EDGE,"E2.sketch_text.stroke-131"),sQuery(id+"F0.wireOp",EDGE,"E2.sketch_text.stroke-132"),sQuery(id+"F0.wireOp",EDGE,"E2.sketch_text.stroke-133"),sQuery(id+"F0.wireOp",EDGE,"E2.sketch_text.stroke-134"),sQuery(id+"F0.wireOp",EDGE,"E2.sketch_text.stroke-135"),sQuery(id+"F0.wireOp",EDGE,"E2.sketch_text.stroke-136"),sQuery(id+"F0.wireOp",EDGE,"E2.sketch_text.stroke-137"),sQuery(id+"F0.wireOp",EDGE,"E2.sketch_text.stroke-138"),sQuery(id+"F0.wireOp",EDGE,"E2.sketch_text.stroke-139"),sQuery(id+"F0.wireOp",EDGE,"E2.sketch_text.stroke-140"),sQuery(id+"F0.wireOp",EDGE,"E2.sketch_text.stroke-141"),sQuery(id+"F0.wireOp",EDGE,"E2.sketch_text.stroke-142"),sQuery(id+"F0.wireOp",EDGE,"E2.sketch_text.stroke-143"),sQuery(id+"F0.wireOp",EDGE,"E2.sketch_text.stroke-144"),sQuery(id+"F0.wireOp",EDGE,"E2.sketch_text.stroke-145"),sQuery(id+"F0.wireOp",EDGE,"E2.sketch_text.stroke-146"),sQuery(id+"F0.wireOp",EDGE,"E2.sketch_text.stroke-147"),sQuery(id+"F0.wireOp",EDGE,"E2.sketch_text.stroke-148"),sQuery(id+"F0.wireOp",EDGE,"E2.sketch_text.stroke-149"),sQuery(id+"F0.wireOp",EDGE,"E2.sketch_text.stroke-150"),sQuery(id+"F0.wireOp",EDGE,"E2.sketch_text.stroke-151"),sQuery(id+"F0.wireOp",EDGE,"E2.sketch_text.stroke-152"),sQuery(id+"F0.wireOp",EDGE,"E2.sketch_text.stroke-153"),sQuery(id+"F0.wireOp",EDGE,"E2.sketch_text.stroke-154"),sQuery(id+"F0.wireOp",EDGE,"E2.sketch_text.stroke-155"),sQuery(id+"F0.wireOp",EDGE,"E2.sketch_text.stroke-156"),sQuery(id+"F0.wireOp",EDGE,"E2.sketch_text.stroke-157"),sQuery(id+"F0.wireOp",EDGE,"E2.sketch_text.stroke-158"),sQuery(id+"F0.wireOp",EDGE,"E2.sketch_text.stroke-159"),sQuery(id+"F0.wireOp",EDGE,"E2.sketch_text.stroke-160"),sQuery(id+"F0.wireOp",EDGE,"E2.sketch_text.stroke-161"),sQuery(id+"F0.wireOp",EDGE,"E2.sketch_text.stroke-162"),sQuery(id+"F0.wireOp",EDGE,"E2.sketch_text.stroke-163"),sQuery(id+"F0.wireOp",EDGE,"E2.sketch_text.stroke-164"),sQuery(id+"F0.wireOp",EDGE,"E2.sketch_text.stroke-165"),sQuery(id+"F0.wireOp",EDGE,"E2.sketch_text.stroke-166"),sQuery(id+"F0.wireOp",EDGE,"E2.sketch_text.stroke-167"),sQuery(id+"F0.wireOp",EDGE,"E2.sketch_text.stroke-168"),sQuery(id+"F0.wireOp",EDGE,"E2.sketch_text.stroke-169"),sQuery(id+"F0.wireOp",EDGE,"E2.sketch_text.stroke-170"),sQuery(id+"F0.wireOp",EDGE,"E2.sketch_text.stroke-171"),sQuery(id+"F0.wireOp",EDGE,"E2.sketch_text.stroke-172"),sQuery(id+"F0.wireOp",EDGE,"E2.sketch_text.stroke-173"),sQuery(id+"F0.wireOp",EDGE,"E2.sketch_text.stroke-174"),sQuery(id+"F0.wireOp",EDGE,"E2.sketch_text.stroke-175"),sQuery(id+"F0.wireOp",EDGE,"E2.sketch_text.stroke-176"),sQuery(id+"F0.wireOp",EDGE,"E2.sketch_text.stroke-177"),sQuery(id+"F0.wireOp",EDGE,"E2.sketch_text.stroke-178"),sQuery(id+"F0.wireOp",EDGE,"E2.sketch_text.stroke-179"),sQuery(id+"F0.wireOp",EDGE,"E2.sketch_text.stroke-180"),sQuery(id+"F0.wireOp",EDGE,"E2.sketch_text.stroke-181"),sQuery(id+"F0.wireOp",EDGE,"E2.sketch_text.stroke-182"),sQuery(id+"F0.wireOp",EDGE,"E2.sketch_text.stroke-183"),sQuery(id+"F0.wireOp",EDGE,"E2.sketch_text.stroke-184"),sQuery(id+"F0.wireOp",EDGE,"E2.sketch_text.stroke-185"),sQuery(id+"F0.wireOp",EDGE,"E2.sketch_text.stroke-186"),sQuery(id+"F0.wireOp",EDGE,"E2.sketch_text.stroke-187"),sQuery(id+"F0.wireOp",EDGE,"E2.sketch_text.stroke-188"),sQuery(id+"F0.wireOp",EDGE,"E2.sketch_text.stroke-189"),sQuery(id+"F0.wireOp",EDGE,"E2.sketch_text.stroke-190"),sQuery(id+"F0.wireOp",EDGE,"E2.sketch_text.stroke-191"),sQuery(id+"F0.wireOp",EDGE,"E2.sketch_text.stroke-192"),sQuery(id+"F0.wireOp",EDGE,"E2.sketch_text.stroke-193"),sQuery(id+"F0.wireOp",EDGE,"E2.sketch_text.stroke-194"),sQuery(id+"F0.wireOp",EDGE,"E2.sketch_text.stroke-195"),sQuery(id+"F0.wireOp",EDGE,"E2.sketch_text.stroke-196"),sQuery(id+"F0.wireOp",EDGE,"E2.sketch_text.stroke-197"),sQuery(id+"F0.wireOp",EDGE,"E2.sketch_text.stroke-198"),sQuery(id+"F0.wireOp",EDGE,"E2.sketch_text.stroke-199"),sQuery(id+"F0.wireOp",EDGE,"E2.sketch_text.stroke-200"),sQuery(id+"F0.wireOp",EDGE,"E2.sketch_text.stroke-201"),sQuery(id+"F0.wireOp",EDGE,"E2.sketch_text.stroke-202"),sQuery(id+"F0.wireOp",EDGE,"E2.sketch_text.stroke-203"),sQuery(id+"F0.wireOp",EDGE,"E2.sketch_text.stroke-204"),sQuery(id+"F0.wireOp",EDGE,"E2.sketch_text.stroke-205"),sQuery(id+"F0.wireOp",EDGE,"E2.sketch_text.stroke-206"),sQuery(id+"F0.wireOp",EDGE,"E2.sketch_text.stroke-207"),sQuery(id+"F0.wireOp",EDGE,"E2.sketch_text.stroke-208"),sQuery(id+"F0.wireOp",EDGE,"E2.sketch_text.stroke-209"),sQuery(id+"F0.wireOp",EDGE,"E2.sketch_text.stroke-210"),sQuery(id+"F0.wireOp",EDGE,"E2.sketch_text.stroke-211"),sQuery(id+"F0.wireOp",EDGE,"E2.sketch_text.stroke-212"),sQuery(id+"F0.wireOp",EDGE,"E2.sketch_text.stroke-213"),sQuery(id+"F0.wireOp",EDGE,"E2.sketch_text.stroke-214"),sQuery(id+"F0.wireOp",EDGE,"E2.sketch_text.stroke-215"),sQuery(id+"F0.wireOp",EDGE,"E2.sketch_text.stroke-216"),sQuery(id+"F0.wireOp",EDGE,"E2.sketch_text.stroke-217"),sQuery(id+"F0.wireOp",EDGE,"E2.sketch_text.stroke-218"),sQuery(id+"F0.wireOp",EDGE,"E2.sketch_text.stroke-219"),sQuery(id+"F0.wireOp",EDGE,"E2.sketch_text.stroke-220"),sQuery(id+"F0.wireOp",EDGE,"E2.sketch_text.stroke-221"),sQuery(id+"F0.wireOp",EDGE,"E2.sketch_text.stroke-222"),sQuery(id+"F0.wireOp",EDGE,"E2.sketch_text.stroke-223"),sQuery(id+"F0.wireOp",EDGE,"E2.sketch_text.stroke-224"),sQuery(id+"F0.wireOp",EDGE,"E2.sketch_text.stroke-225"),sQuery(id+"F0.wireOp",EDGE,"E2.sketch_text.stroke-226"),sQuery(id+"F0.wireOp",EDGE,"E2.sketch_text.stroke-227"),sQuery(id+"F0.wireOp",EDGE,"E2.sketch_text.stroke-228"),sQuery(id+"F0.wireOp",EDGE,"E2.sketch_text.stroke-229"),sQuery(id+"F0.wireOp",EDGE,"E2.sketch_text.stroke-230"),sQuery(id+"F0.wireOp",EDGE,"E2.sketch_text.stroke-231"),sQuery(id+"F0.wireOp",EDGE,"E2.sketch_text.stroke-232"),sQuery(id+"F0.wireOp",EDGE,"E2.sketch_text.stroke-233"),sQuery(id+"F0.wireOp",EDGE,"E2.sketch_text.stroke-234"),sQuery(id+"F0.wireOp",EDGE,"E2.sketch_text.stroke-235"),sQuery(id+"F0.wireOp",EDGE,"E2.sketch_text.stroke-236"),sQuery(id+"F0.wireOp",EDGE,"E2.sketch_text.stroke-237"),sQuery(id+"F0.wireOp",EDGE,"E2.sketch_text.stroke-238"),sQuery(id+"F0.wireOp",EDGE,"E2.sketch_text.stroke-239"),sQuery(id+"F0.wireOp",EDGE,"E2.sketch_text.stroke-240"),sQuery(id+"F0.wireOp",EDGE,"E2.sketch_text.stroke-241"),sQuery(id+"F0.wireOp",EDGE,"E2.sketch_text.stroke-242"),sQuery(id+"F0.wireOp",EDGE,"E2.sketch_text.stroke-243"),sQuery(id+"F0.wireOp",EDGE,"E2.sketch_text.stroke-244"),sQuery(id+"F0.wireOp",EDGE,"E2.sketch_text.stroke-245"),sQuery(id+"F0.wireOp",EDGE,"E2.sketch_text.stroke-246"),sQuery(id+"F0.wireOp",EDGE,"E2.sketch_text.stroke-247"),sQuery(id+"F0.wireOp",EDGE,"E2.sketch_text.stroke-248"),sQuery(id+"F0.wireOp",EDGE,"E2.sketch_text.stroke-249"),sQuery(id+"F0.wireOp",EDGE,"E2.sketch_text.stroke-250"),sQuery(id+"F0.wireOp",EDGE,"E2.sketch_text.stroke-251"),sQuery(id+"F0.wireOp",EDGE,"E2.sketch_text.stroke-252"),sQuery(id+"F0.wireOp",EDGE,"E2.sketch_text.stroke-253"),sQuery(id+"F0.wireOp",EDGE,"E2.sketch_text.stroke-254"),sQuery(id+"F0.wireOp",EDGE,"E2.sketch_text.stroke-255"),sQuery(id+"F0.wireOp",EDGE,"E2.sketch_text.stroke-256"),sQuery(id+"F0.wireOp",EDGE,"E2.sketch_text.stroke-257"),sQuery(id+"F0.wireOp",EDGE,"E2.sketch_text.stroke-258"),sQuery(id+"F0.wireOp",EDGE,"E2.sketch_text.stroke-259"),sQuery(id+"F0.wireOp",EDGE,"E2.sketch_text.stroke-260"),sQuery(id+"F0.wireOp",EDGE,"E2.sketch_text.stroke-261"),sQuery(id+"F0.wireOp",EDGE,"E2.sketch_text.stroke-262"),sQuery(id+"F0.wireOp",EDGE,"E2.sketch_text.stroke-263"),sQuery(id+"F0.wireOp",EDGE,"E2.sketch_text.stroke-264"),sQuery(id+"F0.wireOp",EDGE,"E2.sketch_text.stroke-265"),sQuery(id+"F0.wireOp",EDGE,"E2.sketch_text.stroke-266"),sQuery(id+"F0.wireOp",EDGE,"E2.sketch_text.stroke-267"),sQuery(id+"F0.wireOp",EDGE,"E2.sketch_text.stroke-268"),sQuery(id+"F0.wireOp",EDGE,"E2.sketch_text.stroke-269"),sQuery(id+"F0.wireOp",EDGE,"E2.sketch_text.stroke-270"),sQuery(id+"F0.wireOp",EDGE,"E2.sketch_text.stroke-271"),sQuery(id+"F0.wireOp",EDGE,"E2.sketch_text.stroke-272"),sQuery(id+"F0.wireOp",EDGE,"E2.sketch_text.stroke-273"),sQuery(id+"F0.wireOp",EDGE,"E2.sketch_text.stroke-274"),sQuery(id+"F0.wireOp",EDGE,"E2.sketch_text.stroke-275"),sQuery(id+"F0.wireOp",EDGE,"E2.sketch_text.stroke-276"),sQuery(id+"F0.wireOp",EDGE,"E2.sketch_text.stroke-277"),sQuery(id+"F0.wireOp",EDGE,"E2.sketch_text.stroke-278"),sQuery(id+"F0.wireOp",EDGE,"E2.sketch_text.stroke-279"),sQuery(id+"F0.wireOp",EDGE,"E2.sketch_text.stroke-280"),sQuery(id+"F0.wireOp",EDGE,"E2.sketch_text.stroke-281"),sQuery(id+"F0.wireOp",EDGE,"E2.sketch_text.stroke-282"),sQuery(id+"F0.wireOp",EDGE,"E2.sketch_text.stroke-283"),sQuery(id+"F0.wireOp",EDGE,"E2.sketch_text.stroke-284"),sQuery(id+"F0.wireOp",EDGE,"E2.sketch_text.stroke-285"),sQuery(id+"F0.wireOp",EDGE,"E2.sketch_text.stroke-286"),sQuery(id+"F0.wireOp",EDGE,"E2.sketch_text.stroke-287"),sQuery(id+"F0.wireOp",EDGE,"E2.sketch_text.stroke-288"),sQuery(id+"F0.wireOp",EDGE,"E2.sketch_text.stroke-289"),sQuery(id+"F0.wireOp",EDGE,"E2.sketch_text.stroke-290"),sQuery(id+"F0.wireOp",EDGE,"E2.sketch_text.stroke-291"),sQuery(id+"F0.wireOp",EDGE,"E2.sketch_text.stroke-292"),sQuery(id+"F0.wireOp",EDGE,"E2.sketch_text.stroke-293"),sQuery(id+"F0.wireOp",EDGE,"E2.sketch_text.stroke-294"),sQuery(id+"F0.wireOp",EDGE,"E2.sketch_text.stroke-295"),sQuery(id+"F0.wireOp",EDGE,"E2.sketch_text.stroke-296"),sQuery(id+"F0.wireOp",EDGE,"E2.sketch_text.stroke-297"),sQuery(id+"F0.wireOp",EDGE,"E2.sketch_text.stroke-298"),sQuery(id+"F0.wireOp",EDGE,"E2.sketch_text.stroke-299"),sQuery(id+"F0.wireOp",EDGE,"E2.sketch_text.stroke-300"),sQuery(id+"F0.wireOp",EDGE,"E2.sketch_text.stroke-301"),sQuery(id+"F0.wireOp",EDGE,"E2.sketch_text.stroke-302"),sQuery(id+"F0.wireOp",EDGE,"E2.sketch_text.stroke-303"),sQuery(id+"F0.wireOp",EDGE,"E2.sketch_text.stroke-304"),sQuery(id+"F0.wireOp",EDGE,"E2.sketch_text.stroke-305"),sQuery(id+"F0.wireOp",EDGE,"E2.sketch_text.stroke-306"),sQuery(id+"F0.wireOp",EDGE,"E2.sketch_text.stroke-307"),sQuery(id+"F0.wireOp",EDGE,"E2.sketch_text.stroke-308"),sQuery(id+"F0.wireOp",EDGE,"E2.sketch_text.stroke-309"),sQuery(id+"F0.wireOp",EDGE,"E2.sketch_text.stroke-310"),sQuery(id+"F0.wireOp",EDGE,"E2.sketch_text.stroke-311"),sQuery(id+"F0.wireOp",EDGE,"E2.sketch_text.stroke-312"),sQuery(id+"F0.wireOp",EDGE,"E2.sketch_text.stroke-313"),sQuery(id+"F0.wireOp",EDGE,"E2.sketch_text.stroke-314"),sQuery(id+"F0.wireOp",EDGE,"E2.sketch_text.stroke-315"),sQuery(id+"F0.wireOp",EDGE,"E2.sketch_text.stroke-316"),sQuery(id+"F0.wireOp",EDGE,"E2.sketch_text.stroke-317"),sQuery(id+"F0.wireOp",EDGE,"E2.sketch_text.stroke-318"),sQuery(id+"F0.wireOp",EDGE,"E2.sketch_text.stroke-319"),sQuery(id+"F0.wireOp",EDGE,"E2.sketch_text.stroke-320"),sQuery(id+"F0.wireOp",EDGE,"E2.sketch_text.stroke-321"),sQuery(id+"F0.wireOp",EDGE,"E2.sketch_text.stroke-322"),sQuery(id+"F0.wireOp",EDGE,"E2.sketch_text.stroke-323"),sQuery(id+"F0.wireOp",EDGE,"E2.sketch_text.stroke-324"),sQuery(id+"F0.wireOp",EDGE,"E2.sketch_text.stroke-325"),sQuery(id+"F0.wireOp",EDGE,"E2.sketch_text.stroke-326"),sQuery(id+"F0.wireOp",EDGE,"E2.sketch_text.stroke-327"),sQuery(id+"F0.wireOp",EDGE,"E2.sketch_text.stroke-328"),sQuery(id+"F0.wireOp",EDGE,"E2.sketch_text.stroke-329"),sQuery(id+"F0.wireOp",EDGE,"E2.sketch_text.stroke-330"),sQuery(id+"F0.wireOp",EDGE,"E2.sketch_text.stroke-331"),sQuery(id+"F0.wireOp",EDGE,"E2.sketch_text.stroke-332"),sQuery(id+"F0.wireOp",EDGE,"E2.sketch_text.stroke-333"),sQuery(id+"F0.wireOp",EDGE,"E2.sketch_text.stroke-334"),sQuery(id+"F0.wireOp",EDGE,"E2.sketch_text.stroke-335"),sQuery(id+"F0.wireOp",EDGE,"E2.sketch_text.stroke-336"),sQuery(id+"F0.wireOp",EDGE,"E2.sketch_text.stroke-337"),sQuery(id+"F0.wireOp",EDGE,"E2.sketch_text.stroke-338"),sQuery(id+"F0.wireOp",EDGE,"E2.sketch_text.stroke-339"),sQuery(id+"F0.wireOp",EDGE,"E2.sketch_text.stroke-340"),sQuery(id+"F0.wireOp",EDGE,"E2.sketch_text.stroke-341"),sQuery(id+"F0.wireOp",EDGE,"E2.sketch_text.stroke-342"),sQuery(id+"F0.wireOp",EDGE,"E2.sketch_text.stroke-343"),sQuery(id+"F0.wireOp",EDGE,"E2.sketch_text.stroke-344"),sQuery(id+"F0.wireOp",EDGE,"E2.sketch_text.stroke-345"),sQuery(id+"F0.wireOp",EDGE,"E2.sketch_text.stroke-346"),sQuery(id+"F0.wireOp",EDGE,"E2.sketch_text.stroke-347"),sQuery(id+"F0.wireOp",EDGE,"E2.sketch_text.stroke-348")])],"isStart":false});
            var sketch = newSketch(context, id + "F2", { "sketchPlane" : qUnion([Q0])});
            skLineSegment(sketch, "E3.bottom", {"start": v(-72.26, 66) * mm, "end": v(-62.26, 66) * mm});
            skLineSegment(sketch, "E3.top", {"start": v(-72.26, 56) * mm, "end": v(-62.26, 56) * mm});
            skLineSegment(sketch, "E3.left", {"start": v(-72.26, 66) * mm, "end": v(-72.26, 56) * mm});
            skLineSegment(sketch, "E3.right", {"start": v(-62.26, 66) * mm, "end": v(-62.26, 56) * mm});
            skLineSegment(sketch, "E4.bottom", {"start": v(72.26, 66) * mm, "end": v(62.26, 66) * mm});
            skLineSegment(sketch, "E4.top", {"start": v(72.26, 56) * mm, "end": v(62.26, 56) * mm});
            skLineSegment(sketch, "E4.left", {"start": v(72.26, 66) * mm, "end": v(72.26, 56) * mm});
            skLineSegment(sketch, "E4.right", {"start": v(62.26, 66) * mm, "end": v(62.26, 56) * mm});
            skLineSegment(sketch, "E5.bottom", {"start": v(-72.26, -66) * mm, "end": v(-62.26, -66) * mm});
            skLineSegment(sketch, "E5.top", {"start": v(-72.26, -56) * mm, "end": v(-62.26, -56) * mm});
            skLineSegment(sketch, "E5.left", {"start": v(-72.26, -66) * mm, "end": v(-72.26, -56) * mm});
            skLineSegment(sketch, "E5.right", {"start": v(-62.26, -66) * mm, "end": v(-62.26, -56) * mm});
            skLineSegment(sketch, "E6.bottom", {"start": v(72.26, -66) * mm, "end": v(62.26, -66) * mm});
            skLineSegment(sketch, "E6.top", {"start": v(72.26, -56) * mm, "end": v(62.26, -56) * mm});
            skLineSegment(sketch, "E6.left", {"start": v(72.26, -66) * mm, "end": v(72.26, -56) * mm});
            skLineSegment(sketch, "E6.right", {"start": v(62.26, -66) * mm, "end": v(62.26, -56) * mm});
            skLineSegment(sketch, "E7", {"start": v(-72.26, 66) * mm, "end": v(-62.26, 56) * mm});
            skLineSegment(sketch, "E8", {"start": v(-72.26, -56) * mm, "end": v(-62.26, -66) * mm});
            skLineSegment(sketch, "E9", {"start": v(62.26, 66) * mm, "end": v(72.26, 56) * mm});
            skLineSegment(sketch, "E10", {"start": v(62.26, -56) * mm, "end": v(72.26, -66) * mm});
            skCircle(sketch, "E11", {"center": v(-67.26, 61) * mm, "radius": 1.95 * mm});
            skCircle(sketch, "E12", {"center": v(-67.26, -61) * mm, "radius": 1.95 * mm});
            skCircle(sketch, "E13", {"center": v(67.26, -61) * mm, "radius": 1.95 * mm});
            skCircle(sketch, "E14", {"center": v(67.26, 61) * mm, "radius": 1.95 * mm});
            skSolve(sketch);
        }
        {
            var Q0;
            {var subQ0=sQuery(id+"F2.wireOp",EDGE,"E11");var subQ1=sQuery(id+"F2.wireOp",EDGE,"E7");var subQ2=makeQuery(id+"F2.imprint","INTERSECT",VERTEX,{"disambiguationData":[OD(0.0)],"derivedFrom":[subQ1,subQ0]});Q0=makeQuery(id+"F2.imprint","IMPRINT",FACE,{"disambiguationData":[TD([[makeQuery(id+"F2.imprint","IMPRINT",EDGE,{"disambiguationData":[TD([[subQ2,-1.0]])],"derivedFrom":subQ1}),1.0]])]});}
            var Q1;
            {var subQ0=sQuery(id+"F2.wireOp",EDGE,"E11");var subQ1=sQuery(id+"F2.wireOp",EDGE,"E7");var subQ2=makeQuery(id+"F2.imprint","INTERSECT",VERTEX,{"disambiguationData":[OD(0.0)],"derivedFrom":[subQ1,subQ0]});Q1=makeQuery(id+"F2.imprint","IMPRINT",FACE,{"disambiguationData":[TD([[makeQuery(id+"F2.imprint","IMPRINT",EDGE,{"disambiguationData":[TD([[subQ2,-1.0]])],"derivedFrom":subQ1}),-1.0]])]});}
            var Q2;
            {var subQ0=sQuery(id+"F2.wireOp",EDGE,"E14");var subQ1=sQuery(id+"F2.wireOp",EDGE,"E9");var subQ2=makeQuery(id+"F2.imprint","INTERSECT",VERTEX,{"disambiguationData":[OD(0.0)],"derivedFrom":[subQ1,subQ0]});Q2=makeQuery(id+"F2.imprint","IMPRINT",FACE,{"disambiguationData":[TD([[makeQuery(id+"F2.imprint","IMPRINT",EDGE,{"disambiguationData":[TD([[subQ2,-1.0]])],"derivedFrom":subQ1}),1.0]])]});}
            var Q3;
            {var subQ0=sQuery(id+"F2.wireOp",EDGE,"E14");var subQ1=sQuery(id+"F2.wireOp",EDGE,"E9");var subQ2=makeQuery(id+"F2.imprint","INTERSECT",VERTEX,{"disambiguationData":[OD(0.0)],"derivedFrom":[subQ1,subQ0]});Q3=makeQuery(id+"F2.imprint","IMPRINT",FACE,{"disambiguationData":[TD([[makeQuery(id+"F2.imprint","IMPRINT",EDGE,{"disambiguationData":[TD([[subQ2,-1.0]])],"derivedFrom":subQ1}),-1.0]])]});}
            var Q4;
            {var subQ0=sQuery(id+"F2.wireOp",EDGE,"E12");var subQ1=sQuery(id+"F2.wireOp",EDGE,"E8");var subQ2=makeQuery(id+"F2.imprint","INTERSECT",VERTEX,{"disambiguationData":[OD(0.0)],"derivedFrom":[subQ1,subQ0]});Q4=makeQuery(id+"F2.imprint","IMPRINT",FACE,{"disambiguationData":[TD([[makeQuery(id+"F2.imprint","IMPRINT",EDGE,{"disambiguationData":[TD([[subQ2,-1.0]])],"derivedFrom":subQ1}),1.0]])]});}
            var Q5;
            {var subQ0=sQuery(id+"F2.wireOp",EDGE,"E12");var subQ1=sQuery(id+"F2.wireOp",EDGE,"E8");var subQ2=makeQuery(id+"F2.imprint","INTERSECT",VERTEX,{"disambiguationData":[OD(0.0)],"derivedFrom":[subQ1,subQ0]});Q5=makeQuery(id+"F2.imprint","IMPRINT",FACE,{"disambiguationData":[TD([[makeQuery(id+"F2.imprint","IMPRINT",EDGE,{"disambiguationData":[TD([[subQ2,-1.0]])],"derivedFrom":subQ1}),-1.0]])]});}
            var Q6;
            {var subQ0=sQuery(id+"F2.wireOp",EDGE,"E13");var subQ1=sQuery(id+"F2.wireOp",EDGE,"E10");var subQ2=makeQuery(id+"F2.imprint","INTERSECT",VERTEX,{"disambiguationData":[OD(0.0)],"derivedFrom":[subQ1,subQ0]});Q6=makeQuery(id+"F2.imprint","IMPRINT",FACE,{"disambiguationData":[TD([[makeQuery(id+"F2.imprint","IMPRINT",EDGE,{"disambiguationData":[TD([[subQ2,-1.0]])],"derivedFrom":subQ1}),-1.0]])]});}
            var Q7;
            {var subQ0=sQuery(id+"F2.wireOp",EDGE,"E13");var subQ1=sQuery(id+"F2.wireOp",EDGE,"E10");var subQ2=makeQuery(id+"F2.imprint","INTERSECT",VERTEX,{"disambiguationData":[OD(0.0)],"derivedFrom":[subQ1,subQ0]});Q7=makeQuery(id+"F2.imprint","IMPRINT",FACE,{"disambiguationData":[TD([[makeQuery(id+"F2.imprint","IMPRINT",EDGE,{"disambiguationData":[TD([[subQ2,-1.0]])],"derivedFrom":subQ1}),1.0]])]});}
            extrude(context, id + "F3", {"entities" : qUnion([Q0, Q1, Q2, Q3, Q4, Q5, Q6, Q7]), "operationType" : NewBodyOperationType.REMOVE, "oppositeDirection" : true, "depth" : 4 * mm, "offsetDistance" : 25 * mm});
        }
    });
